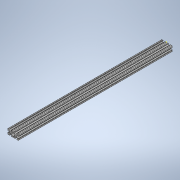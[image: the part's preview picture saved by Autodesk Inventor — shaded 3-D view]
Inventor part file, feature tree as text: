
AUTODESK INVENTOR PART (.ipt)
format: ipt  version: 2020 (Build 240168000, 168)  size: 331,776 bytes
history: native  units: in
note: dims shown in document units (in); Inventor stores cm internally (conversion verified against a paired STEP export)
features: sketch x2, extrude x1
ambient origin geometry x8: Origin, YZ Plane, XZ Plane, XY Plane, X Axis, Y Axis, Z Axis, Center Point
bodies: Solid1 (feature_tree)
feature tree (3):
  extrude  "Extrusion1"  [1 undecoded]
  sketch  "Sketch2"
  sketch  "Sketch1"  dims[d0=28.0in d1=0.0in]
note: 1 required parameter value undecoded (feature->parameter linkage not recoverable at this tier; creation-order binding heuristic only, values carry confidence <= 0.55)
